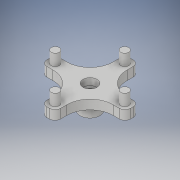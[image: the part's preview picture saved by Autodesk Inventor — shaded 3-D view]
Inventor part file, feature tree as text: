
AUTODESK INVENTOR PART (.ipt)
format: ipt  version: 2019 (Build 230136000, 136)  size: 220,160 bytes
history: native  units: in
note: dims shown in document units (in); Inventor stores cm internally (conversion verified against a paired STEP export)
features: extrude x9, sketch x7
ambient origin geometry x8: Origin, YZ Plane, XZ Plane, XY Plane, X Axis, Y Axis, Z Axis, Center Point
bodies: Solid1 (feature_tree)
feature tree (16):
  sketch  "Sketch1"  dims[d1=1.5748in d3=1.5748in d4=360.0deg d5=0.175in d6=360.0deg d7=0.125in d8=0.2in d9=0.0in d10=0.45in d11=0.0in]
  extrude  "Extrusion1"  Depth=0.45in TaperAngle=0.0deg
  extrude  "Extrusion2"  Depth=0.45in TaperAngle=360.0deg
  extrude  "Extrusion3"  Depth=0.45in TaperAngle=0.0deg
  extrude  "Extrusion4"  Depth=0.1in
  extrude  "Extrusion5"  Depth=0.3in
  extrude  "Extrusion6"  Depth=0.25in
  extrude  "Extrusion7"  Depth=0.15in
  extrude  "Extrusion8"  Depth=0.1in TaperAngle=0.0deg
  extrude  "Extrusion9"  Depth=0.1in TaperAngle=0.0deg
  sketch  "Sketch2"  dims[d12=0.45in d13=0.0in d14=1.5748in d16=360.0deg]
  sketch  "Sketch3"  dims[d18=0.225in d19=0.45in d20=0.0in]
  sketch  "Sketch4"  dims[d21=0.1in d22=0.225in]
  sketch  "Sketch5"  dims[d23=0.2in d24=0.0in d25=0.3in]
  sketch  "Sketch6"  dims[d26=0.15in d27=0.0in d28=0.25in]
  sketch  "Sketch7"  dims[d29=2.0in d30=0.0in d31=0.15in d32=0.1in d33=0.0in d34=0.1in d35=0.0in]
